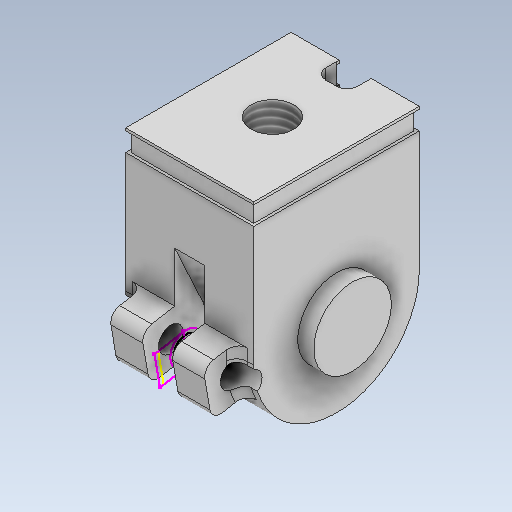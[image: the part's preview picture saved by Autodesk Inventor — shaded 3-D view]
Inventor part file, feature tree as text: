
AUTODESK INVENTOR PART (.ipt)
format: ipt  version: 2021 (Build 250183000, 183)  size: 532,992 bytes
history: native  units: mm
features: sketch x21, extrude x14, plane x7, other x4, fillet x4, hole x2, thread x2, revolve x1, shell x1, sweep x1
ambient origin geometry x8: Origin, YZ Plane, XZ Plane, XY Plane, X Axis, Y Axis, Z Axis, Center Point
bodies: Body1 (feature_tree)
feature tree (57):
  other  "Sólido1"
  revolve  "Revolución1"  [1 undecoded]
  shell  "Vaciado1"  Thickness=90.0deg
  extrude  "Extrusión1"  Depth=10.0mm
  extrude  "Extrusión2"  TaperAngle=0.0deg  [1 undecoded]
  sketch  "Boceto4"  dims[d16=2.0mm d17=8.0mm]
  plane  "Plano de trabajo4"
  sketch  "Boceto6"  dims[d20=8.0mm d22=20.0mm]
  plane  "Plano de trabajo1"
  sketch  "Boceto7"  dims[d23=5.0mm d24=0.0mm d25=12.0mm]
  sweep  "Barrido2"
  extrude  "Extrusión5"  Depth=20.0mm
  extrude  "Extrusión6"  Depth=12.0mm
  plane  "Plano de trabajo2"
  sketch  "Boceto12"  dims[d57=18.0mm d60=10.0mm]
  extrude  "Extrusión8"  Depth=4.0mm
  fillet  "Empalme3"  Radius=2.0mm
  extrude  "Extrusión9"  Depth=2.0mm
  extrude  "Extrusión10"  Depth=26.0mm
  plane  "Plano de trabajo3"
  extrude  "Extrusión11"  Depth=10.0mm
  hole  "Agujero1"  [1 undecoded]
  plane  "Plano de trabajo5"
  plane  "Plano de trabajo6"
  extrude  "Extrusión12"  Depth=0.5mm
  hole  "Agujero2"  [1 undecoded]
  thread  "Rosca2"  [1 undecoded]
  thread  "Rosca3"  [1 undecoded]
  extrude  "Extrusión14"  Depth=7.25mm
  fillet  "Empalme4"  Radius=11.25mm
  sketch  "Boceto23"  dims[d100=34.0mm d103=8.5mm d104=25.0mm d106=20.0mm]
  plane  "Plano de trabajo7"
  extrude  "Extrusión17"  TaperAngle=0.0deg  [1 undecoded]
  extrude  "Extrusión18"  Depth=9.5mm
  extrude  "Extrusión19"  Depth=0.5mm
  extrude  "Extrusión20"  Depth=8.5mm
  fillet  "Empalme5"  Radius=25.0mm
  fillet  "Empalme6"  Radius=20.0mm
  sketch  "Boceto1"  dims[d1=0.0mm d3=34.0mm d4=90.0deg]
  sketch  "Boceto3"  dims[d13=40.0mm d14=0.0mm]
  sketch  "Boceto 3D1"  dims[d7=10.0mm d12=2.0mm]
  other  "Intersección 3D1"
  sketch  "Boceto8"  dims[d26=5.0mm d34=4.0mm d35=2.0mm]
  sketch  "Boceto9"  dims[d36=1.5mm d46=2.0mm d48=8.0mm d49=8.0mm]
  sketch  "Boceto10"  dims[d55=9.0mm d56=26.0mm]
  other  "Intersección 3D4"
  other  "Intersección 3D6"
  sketch  "Boceto13"  dims[d61=26.0mm d70=2.0mm]
  sketch  "Boceto14"  dims[d71=1.0mm d72=0.5mm]
  sketch  "Boceto15"  dims[d73=0.5mm d78=0.0mm d79=0.0mm d82=7.75mm d84=12.0mm]
  sketch  "Boceto16"  dims[d85=0.0mm d86=7.25mm d87=11.25mm]
  sketch  "Boceto17"  dims[d88=15.0mm d89=0.0mm]
  sketch  "Boceto18"  dims[d94=8.5mm d95=9.5mm]
  sketch  "Boceto21"  dims[d98=0.5mm d99=0.5mm]
  sketch  "Boceto24"  dims[d107=32.599342mm]
  sketch  "Boceto25"  dims[d115=11.25mm]
  sketch  "Boceto26"  dims[d116=0.0mm d117=11.25mm d118=8.25mm d119=29.697249mm d120=2.3mm d121=11.25mm d122=8.25mm d123=29.697249mm d124=2.8mm d125=2.4mm d126=2.4mm d127=2.4mm d128=8.8mm d129=0.0mm d130=1.0mm d131=6.6mm d132=3.3mm d133=3.0mm d134=6.6mm d135=2.8mm d136=0.0mm d137=15.0deg d138=1.5mm d139=16.0mm d140=1.5mm d141=1.0mm d143=3.0mm d144=3.0mm d145=3.0mm d146=3.0mm d147=6.0mm d148=0.0mm d149=10.0mm d150=9.0mm d151=4.0mm d152=0.5mm d153=0.0mm d154=2.0mm d155=2.0mm d156=6.0mm d157=4.0mm d158=2.0mm d159=90.0deg d160=8.0mm d161=0.0mm d162=-3.0mm d163=19.0mm d164=8.0mm d165=6.0mm d166=0.0mm d167=8.0mm d168=4.0mm d169=6.0mm d170=8.0mm d171=2.0mm d172=90.0deg d173=20.0mm d174=0.0mm d175=19.0mm d176=0.0mm d177=7.0mm d178=0.0mm d185=11.25mm d186=8.25mm d187=29.697249mm d188=2.3mm d189=4.3mm d190=0.0mm d191=1.0mm d201=11.25mm d202=8.25mm d203=29.697249mm d204=2.3mm d205=2.4mm d206=2.4mm d209=-2.0mm d210=60.0mm d211=60.0mm d212=84.0mm d213=0.0mm d214=11.5mm d215=15.0mm d216=60.0mm d217=60.0mm d218=2.0mm d219=0.0mm d220=12.0mm d221=15.5mm d222=0.25mm d223=0.0mm d224=5.0mm d226=3.0mm d227=3.0mm d228=1.0mm d229=8.0mm d230=0.0mm d231=4.0mm d232=4.0mm d234=7.0mm d235=1.5mm d236=0.0mm d237=1.5mm]
note: 7 required parameter values undecoded (feature->parameter linkage not recoverable at this tier; creation-order binding heuristic only, values carry confidence <= 0.55)